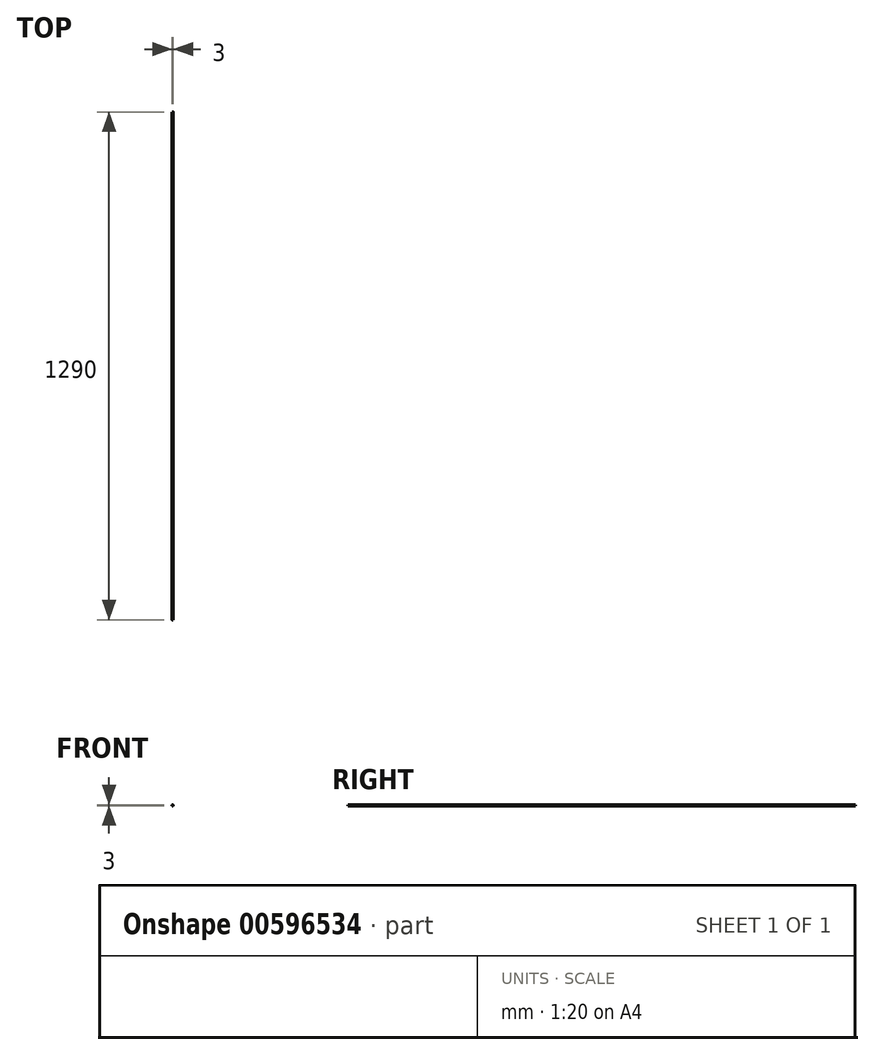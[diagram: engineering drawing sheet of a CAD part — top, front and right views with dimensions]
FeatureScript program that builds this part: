
annotation { "Feature Type Name" : "Feature", "Feature Type Description" : "" }
export const myFeature = defineFeature(function(context is Context, id is Id, definition is map)
    precondition{}
    {
        {
            var Q0;
            Q0=qCreatedBy(makeId("Front.planeOp"),FACE);
            var sketch = newSketch(context, id + "F0", { "sketchPlane" : qUnion([Q0])});
            skCircle(sketch, "E0", {"center": v(0, 0) * mm, "radius": 1.5 * mm});
            skSolve(sketch);
        }
        {
            var Q0;
            Q0=makeQuery(id+"F0.imprint","IMPRINT",FACE,{"disambiguationData":[TD([[makeQuery(id+"F0.imprint","IMPRINT",EDGE,{"derivedFrom":sQuery(id+"F0.wireOp",EDGE,"E0")}),1.0]])]});
            extrude(context, id + "F1", {"entities" : qUnion([Q0]), "depth" : 1290 * mm, "offsetDistance" : 25 * mm});
        }
    });
